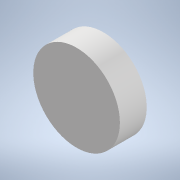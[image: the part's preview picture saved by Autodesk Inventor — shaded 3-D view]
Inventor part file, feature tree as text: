
AUTODESK INVENTOR PART (.ipt)
format: ipt  version: 2020 (Build 240168000, 168)  size: 90,624 bytes
history: native  units: in
note: dims shown in document units (in); Inventor stores cm internally (conversion verified against a paired STEP export)
features: other x3, sketch x1, plane x1, extrude x1, reference x1
ambient origin geometry x8: Origin, YZ Plane, XZ Plane, XY Plane, X Axis, Y Axis, Z Axis, Center Point
bodies: Solid1 (feature_tree)
feature tree (7):
  sketch  "Sketch1"  dims[d0=1.0in d1=0.0in]
  plane  "Work Plane1"
  extrude  "Extrusion1"  [1 undecoded]
  reference  "Reference1"
  other  "<userpath>\Documents\FRC\2020\am-2256 4 in HiGrip Wheel.iam"
  other  "am-2256 4 in HiGrip Wheel.iam"
  other  "4 in tread_2"
note: 1 required parameter value undecoded (feature->parameter linkage not recoverable at this tier; creation-order binding heuristic only, values carry confidence <= 0.55)
